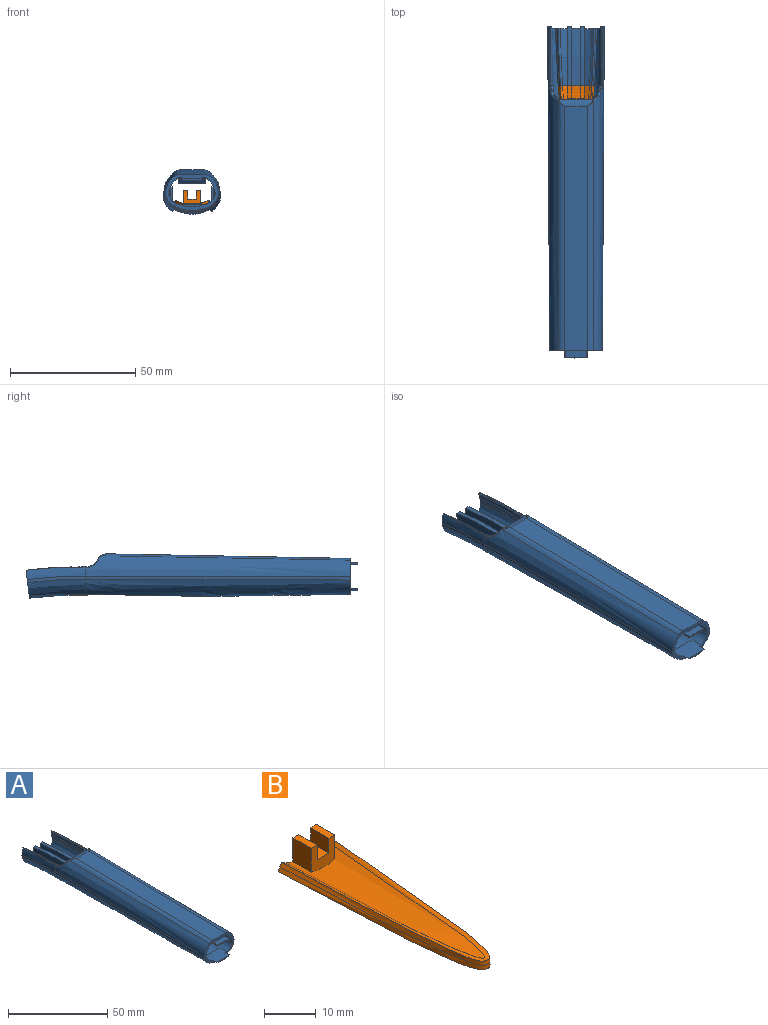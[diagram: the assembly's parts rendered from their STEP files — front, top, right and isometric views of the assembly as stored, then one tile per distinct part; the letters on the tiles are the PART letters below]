
ASSEMBLY  parts=2 mates=1
PART A: 134 faces, bbox 27x265.1x35.1 mm
  f0: bspline ~32.11x20.92mm, area 5.6mm2, adj f29,f36,f40,f76
  f1: plane 35.08x16.95mm, normal (0,0.02,-1), area 310.9mm2, adj f3,f5,f18,f20,f22,f67,f68,f70
  f2: plane 58.23x10.94mm, normal (0,0.02,-1), area 594.8mm2, adj f3,f5,f56,f57,f58,f60,f66
  f3: bspline ~105.7x8.16mm, area 859mm2, adj f1,f2,f4,f12,f13,f21,f22,f30
  f4: bspline ~228.99x1.34mm, area 68.2mm2, adj f3,f50,f56,f105
  f5: bspline ~105.7x8.16mm, area 859.1mm2, adj f1,f2,f6,f15,f16,f19,f20,f34
  f6: bspline ~85.15x0.93mm, area 68.2mm2, adj f5,f42,f56,f105
  f7: plane 97.19x9.34mm, normal (0,-0.02,1), area 895.6mm2, adj f10,f11,f18,f56
  f8: bspline ~228.99x9.18mm, area 873.6mm2, adj f11,f23,f24,f36,f56,f103
  f9: bspline ~105.7x8.28mm, area 873.5mm2, adj f10,f26,f27,f32,f56,f104
  f10: bspline ~141.43x3.43mm, area 259.1mm2, adj f7,f9,f28,f56
  f11: bspline ~141.43x3.43mm, area 259.1mm2, adj f7,f8,f25,f56
  f12: bspline ~228.99x1.34mm, area 19.6mm2, adj f3,f35,f52,f105
  f13: plane 2.29x0.93mm, normal (0,1,0), area 0.6mm2, adj f3,f14,f21,f23,f39,f40
  f14: cylinder r=5.4mm len=4.85mm, axis (-1,0,0), area 2.1mm2, adj f13,f18,f21,f23
  f15: plane 2.29x0.93mm, normal (0,1,0), area 0.6mm2, adj f5,f17,f19,f26,f38,f41
  f16: bspline ~228.99x1.34mm, area 19.6mm2, adj f5,f33,f45,f105
  f17: cylinder r=5.4mm len=4.85mm, axis (-1,0,0), area 2.1mm2, adj f15,f18,f19,f26
  f18: cylinder r=4mm len=16.08mm, axis (-1,0,0), area 40.3mm2, adj f1,f7,f14,f17,f20,f22,f24,f25
  f19: bspline ~6.36x4.3mm, area 6.3mm2, adj f5,f15,f17,f20
  f20: bspline ~3.28x2.53mm, area 2.3mm2, adj f1,f5,f18,f19
  f21: bspline ~6.36x4.3mm, area 6.3mm2, adj f3,f13,f14,f22
  f22: bspline ~3.42x2.68mm, area 2.3mm2, adj f1,f3,f18,f21
  f23: bspline ~6.57x4.71mm, area 4.1mm2, adj f8,f13,f14,f24,f29
  f24: bspline ~2.91x2.89mm, area 1.2mm2, adj f8,f18,f23,f25
  f25: bspline ~2.61x2.59mm, area 0.5mm2, adj f11,f18,f24
  f26: bspline ~6.57x4.71mm, area 4.1mm2, adj f9,f15,f17,f27,f31
  f27: bspline ~2.91x2.89mm, area 1.2mm2, adj f9,f18,f26,f28
  f28: bspline ~2.52x2.5mm, area 0.5mm2, adj f10,f18,f27
  f29: plane 0.41x0.34mm, normal (0,-1,0), area 0mm2, adj f0,f23,f36,f40
  f30: bspline ~23.58x3.47mm, area 44.4mm2, adj f3,f35,f39,f76
  f31: plane 0.41x0.34mm, normal (0,-1,0), area 0mm2, adj f26,f32,f37,f41
  f32: bspline ~32.11x6.34mm, area 91.7mm2, adj f9,f31,f37,f76,f124
  f33: bspline ~31.46x3.53mm, area 22.3mm2, adj f16,f34,f76,f128
  f34: bspline ~31.89x5.15mm, area 44.4mm2, adj f5,f33,f38,f76
  f35: bspline ~31.46x3.53mm, area 22.2mm2, adj f12,f30,f76,f122
  f36: bspline ~32.11x6.34mm, area 91.8mm2, adj f0,f8,f29,f76,f121
  f37: bspline ~32.11x20.92mm, area 5.6mm2, adj f31,f32,f41,f76
  f38: plane 23.86x2.59mm, normal (-1,0,0), area 33.8mm2, adj f15,f34,f41,f76
  f39: plane 23.86x2.59mm, normal (1,0,0), area 33.8mm2, adj f13,f30,f40,f76
  f40: bspline ~28.88x2.28mm, area 18.7mm2, adj f0,f13,f29,f39,f76
  f41: bspline ~28.88x2.28mm, area 18.7mm2, adj f15,f31,f37,f38,f76
  f42: plane 7.63x1.35mm, normal (0,-0.17,-0.98), area 7.1mm2, adj f5,f6,f43,f44,f45
  f43: plane 8.46x4.78mm, normal (-1,0,0), area 12mm2, adj f5,f42,f44,f45,f46,f47,f48
  f44: plane 3.3x0.89mm, normal (0,-0.98,0.17), area 1.8mm2, adj f5,f42,f43
  f45: plane 4.8x0.96mm, normal (0,0.98,-0.17), area 3.3mm2, adj f5,f16,f42,f43
  f46: plane 2.44x0.78mm, normal (0,0.98,-0.17), area 1.1mm2, adj f5,f43,f47
  f47: plane 6.27x1.11mm, normal (0,0.17,0.98), area 5.5mm2, adj f5,f43,f46,f48
  f48: plane 3.67x0.95mm, normal (0,-0.98,0.17), area 2.2mm2, adj f5,f43,f47
  f49: plane 8.46x4.78mm, normal (1,0,0), area 12mm2, adj f3,f50,f51,f52,f53,f54,f55
  f50: plane 7.63x1.35mm, normal (0,-0.17,-0.98), area 7.1mm2, adj f3,f4,f49,f51,f52
  f51: plane 3.3x0.89mm, normal (0,-0.98,0.17), area 1.8mm2, adj f3,f49,f50
  f52: plane 4.8x0.96mm, normal (0,0.98,-0.17), area 3.3mm2, adj f3,f12,f49,f50
  f53: plane 2.44x0.78mm, normal (0,0.98,-0.17), area 1.1mm2, adj f3,f49,f54
  f54: plane 6.27x1.11mm, normal (0,0.17,0.98), area 5.5mm2, adj f3,f49,f53,f55
  f55: plane 3.67x0.95mm, normal (0,-0.98,0.17), area 2.2mm2, adj f3,f49,f54
  f56: plane 24.01x17.36mm, normal (0,-1,0), area 74.5mm2, adj f2,f3,f4,f5,f6,f7,f8,f9
  f57: plane 8x1.09mm, normal (1,0,0), area 7.3mm2, adj f2,f56,f59,f60,f61,f62
  f58: plane 8x1.09mm, normal (-1,0,0), area 7.3mm2, adj f2,f56,f59,f60,f61,f62
  f59: plane 8x8mm, normal (0,0,-1), area 64mm2, adj f57,f58,f60,f62
  f60: plane 8x1.09mm, normal (0,1,0), area 8.8mm2, adj f2,f57,f58,f59
  f61: plane 8x3mm, normal (0,0,1), area 24mm2, adj f56,f57,f58,f62
  f62: plane 8x0.7mm, normal (0,-1,0), area 5.6mm2, adj f57,f58,f59,f61
  f63: plane 10.41x3.81mm, normal (-1,0,0), area 20.7mm2, adj f3,f64,f66,f67
  f64: plane 10.86x0.5mm, normal (0,0,-1), area 5.4mm2, adj f63,f65,f66,f67
  f65: plane 10.41x3.81mm, normal (1,0,0), area 20.7mm2, adj f5,f64,f66,f67
  f66: plane 10.87x9.9mm, normal (0,-0.34,-0.94), area 114.5mm2, adj f2,f63,f64,f65
  f67: plane 10.86x3.8mm, normal (0,1,0), area 17mm2, adj f1,f63,f64,f65,f68,f72
  f68: cylinder r=1.99mm len=12mm, axis (0,-1,0), area 135.3mm2, adj f1,f67,f70
  f69: cylinder r=1.75mm len=12mm, axis (0,-1,0), area 131.9mm2, adj f70,f71
  f70: plane 3.98x3.97mm, normal (0,1,0), area 2.8mm2, adj f1,f68,f69
  f71: plane 3.5x3.5mm, normal (0,1,0), area 9.6mm2, adj f69
  f72: cylinder r=1.99mm len=12mm, axis (0,-1,0), area 135.3mm2, adj f1,f67,f74
  f73: cylinder r=1.75mm len=12mm, axis (0,-1,0), area 131.9mm2, adj f74,f75
  f74: plane 3.98x3.97mm, normal (0,1,0), area 2.8mm2, adj f1,f72,f73
  f75: plane 3.5x3.5mm, normal (0,1,0), area 9.6mm2, adj f73
  f76: plane 23.73x12.13mm, normal (0,0.99,-0.13), area 90.5mm2, adj f0,f30,f32,f33,f34,f35,f36,f37
  f77: plane 6x1.06mm, normal (0,-0.17,-0.98), area 3.7mm2, adj f78,f88,f89,f90
  f78: plane 6.17x2.01mm, normal (-0.77,0.11,0.63), area 7.7mm2, adj f77,f79,f88,f90
  f79: plane 6x1.06mm, normal (0,0.17,0.98), area 3.6mm2, adj f78,f88,f90,f91
  f80: plane 6x1.06mm, normal (0,0.17,0.98), area 3.6mm2, adj f81,f92,f93,f94
  f81: plane 6.17x2.01mm, normal (0.77,0.11,0.63), area 7.7mm2, adj f80,f82,f92,f94
  f82: plane 6x1.06mm, normal (0,-0.17,-0.98), area 3.7mm2, adj f81,f92,f94,f95
  f83: plane 9.28x0.85mm, normal (0,-1,0), area 5.3mm2, adj f84,f97
  f84: extruded ~9.28x3mm, area 28.5mm2, adj f56,f83,f97
  f85: plane 1.05x0.03mm, normal (-1,0,0), area 0mm2, adj f86,f99,f100
  f86: offset ~230.99x17.57mm, area 401.1mm2, adj f85,f87,f98,f99,f100,f101
  f87: bspline ~11.21x7.08mm, area 0mm2, adj f86,f99,f101
  f88: plane 5.55x1.44mm, normal (0,0.98,-0.17), area 4.3mm2, adj f77,f78,f79,f89,f91,f105
  f89: plane 6.82x4.72mm, normal (-1,0,0), area 25.7mm2, adj f77,f88,f90,f105
  f90: plane 6.53x1.44mm, normal (0,-0.98,0.17), area 5.1mm2, adj f77,f78,f79,f89,f91,f105
  f91: plane 7.15x6.57mm, normal (1,0,0), area 37.2mm2, adj f79,f88,f90,f105
  f92: plane 5.55x1.44mm, normal (0,0.98,-0.17), area 4.3mm2, adj f80,f81,f82,f93,f95,f105
  f93: plane 7.15x6.57mm, normal (-1,0,0), area 37.2mm2, adj f80,f92,f94,f105
  f94: plane 6.54x1.44mm, normal (0,-0.98,0.17), area 5.1mm2, adj f80,f81,f82,f93,f95,f105
  f95: plane 6.82x4.72mm, normal (1,0,0), area 25.7mm2, adj f82,f92,f94,f105
  f96: plane 11.24x1.13mm, normal (0,1,0), area 8.7mm2, adj f97,f105
  f97: plane 11.24x8mm, normal (0,0,1), area 83.4mm2, adj f56,f83,f84,f96,f105
  f98: bspline ~56.35x13.51mm, area 99mm2, adj f86,f102,f105,f106
  f99: plane 7.16x6.4mm, normal (0,-1,0), area 33.7mm2, adj f85,f86,f87,f111,f112,f113,f114,f131
  f100: bspline ~2.99x2.01mm, area 2.7mm2, adj f85,f86,f107,f123
  f101: bspline ~3.05x2.05mm, area 2.8mm2, adj f86,f87,f108,f129
  f102: bspline ~1.39x1.39mm, area 1mm2, adj f98,f105,f107,f117
  f103: bspline ~228.99x1.71mm, area 140.7mm2, adj f8,f56,f109,f121
  f104: bspline ~228.99x1.71mm, area 140.7mm2, adj f9,f56,f109,f124
  f105: bspline ~105.7x19.67mm, area 2007.8mm2, adj f4,f6,f12,f16,f56,f88,f89,f90
  f106: bspline ~1.39x1.39mm, area 1mm2, adj f98,f105,f108,f127
  f107: bspline ~1.38x1.38mm, area 1mm2, adj f100,f102,f115,f116
  f108: bspline ~1.38x1.38mm, area 1mm2, adj f101,f106,f125,f126
  f109: bspline ~105.7x22.25mm, area 2448.7mm2, adj f56,f103,f104,f118,f120,f130
  f110: bspline ~228.99x15.57mm, area 444.2mm2, adj f118,f119
  f111: plane 23.42x4.77mm, normal (-1,0,0), area 81.3mm2, adj f76,f99,f112,f133
  f112: bspline ~31.04x3.2mm, area 73.7mm2, adj f76,f99,f111,f113
  f113: plane 23.42x4.77mm, normal (1,0,0), area 81.3mm2, adj f76,f99,f112,f114
  f114: bspline ~31.61x2.6mm, area 37.5mm2, adj f76,f99,f113,f131
  f115: offset ~28x4.01mm, area 23mm2, adj f76,f107,f116,f123
  f116: bspline ~25.76x1.8mm, area 23mm2, adj f76,f107,f115,f117
  f117: offset ~28.28x3.89mm, area 21.6mm2, adj f76,f102,f105,f116,f122
  f118: extruded ~71.85x28.66mm, area 193.5mm2, adj f76,f109,f110,f119,f120,f130
  f119: bspline ~30.89x18.04mm, area 337.3mm2, adj f76,f110,f118
  f120: bspline ~23.16x7.13mm, area 165.1mm2, adj f76,f109,f118,f121
  f121: bspline ~31.48x3.78mm, area 28.4mm2, adj f36,f76,f103,f120
  f122: bspline ~23.18x5.28mm, area 98.7mm2, adj f35,f76,f105,f117
  f123: offset ~35x11.55mm, area 68.4mm2, adj f76,f100,f115,f131
  f124: bspline ~23.31x2.49mm, area 28.5mm2, adj f32,f76,f104,f130
  f125: offset ~28.01x4.02mm, area 23mm2, adj f76,f108,f126,f129
  f126: bspline ~25.45x1.91mm, area 23mm2, adj f76,f108,f125,f127
  f127: offset ~24.84x3.64mm, area 21.6mm2, adj f76,f105,f106,f126,f128
  f128: bspline ~31.31x7.67mm, area 97.2mm2, adj f33,f76,f105,f127
  f129: offset ~35x11.55mm, area 69.6mm2, adj f76,f101,f125,f132
  f130: bspline ~31.28x9.39mm, area 163.7mm2, adj f76,f109,f118,f124
  f131: plane 24.12x7.67mm, normal (-1,0,0), area 130.9mm2, adj f76,f99,f114,f123
  f132: bspline ~31.61x9.4mm, area 131.9mm2, adj f76,f99,f129,f133
  f133: bspline ~31.61x2.6mm, area 37.5mm2, adj f76,f99,f111,f132
PART B: 29 faces, bbox 19.6x234.9x12.2 mm
  f0: bspline ~0.97x0.26mm, area 0mm2, adj f1,f4,f5,f6
  f1: bspline ~2.99x2.01mm, area 2.8mm2, adj f0,f5,f6,f9
  f2: bspline ~3.05x2.05mm, area 2.9mm2, adj f3,f5,f6,f7
  f3: bspline ~0.97x0.26mm, area 0mm2, adj f2,f4,f5,f6
  f4: bspline ~6.4x1.38mm, area 6.2mm2, adj f0,f3,f5,f19
  f5: offset ~151.53x19.57mm, area 337.7mm2, adj f0,f1,f2,f3,f4,f8,f20,f26
  f6: offset ~230.99x17.57mm, area 371.1mm2, adj f0,f1,f2,f3,f13,f16,f17,f18
  f7: bspline ~1.38x1.38mm, area 1mm2, adj f2,f8,f10,f14
  f8: bspline ~49.81x12.56mm, area 100.5mm2, adj f5,f7,f9,f10
  f9: bspline ~1.38x1.38mm, area 1mm2, adj f1,f8,f10,f12
  f10: offset ~52.81x14.13mm, area 101.5mm2, adj f7,f8,f9,f11
  f11: bspline ~49.83x14.68mm, area 102.4mm2, adj f10,f12,f14,f15
  f12: bspline ~1.38x1.38mm, area 1mm2, adj f9,f11,f13,f15
  f13: bspline ~48.89x12.98mm, area 100mm2, adj f6,f12,f14,f15
  f14: bspline ~1.38x1.38mm, area 1mm2, adj f7,f11,f13,f15
  f15: offset ~51.82x15.62mm, area 100.7mm2, adj f11,f12,f13,f14
  f16: plane 6.41x0.5mm, normal (0,-1,0), area 0.4mm2, adj f6,f17,f18,f19
  f17: plane 5x0.07mm, normal (-1,0,0), area 0.2mm2, adj f6,f16,f19
  f18: plane 5x0.07mm, normal (1,0,0), area 0.2mm2, adj f6,f16,f19
  f19: extruded ~6.4x5mm, area 32.4mm2, adj f4,f16,f17,f18
  f20: plane 5.7x5mm, normal (1,0,0), area 28.3mm2, adj f5,f21,f27,f28
  f21: plane 5x1.6mm, normal (0,0,1), area 8mm2, adj f20,f22,f27,f28
  f22: plane 5x3.5mm, normal (-1,0,0), area 17.5mm2, adj f21,f23,f27,f28
  f23: plane 5x3.2mm, normal (0,0,1), area 16mm2, adj f22,f24,f27,f28
  f24: plane 5x3.5mm, normal (1,0,0), area 17.5mm2, adj f23,f25,f27,f28
  f25: plane 5x1.6mm, normal (0,0,1), area 8mm2, adj f24,f26,f27,f28
  f26: plane 5.7x5mm, normal (-1,0,0), area 28.3mm2, adj f5,f25,f27,f28
  f27: plane 6.4x6.09mm, normal (0,-1,0), area 26.8mm2, adj f5,f20,f21,f22,f23,f24,f25,f26
  f28: plane 6.4x6.16mm, normal (0,1,0), area 27.2mm2, adj f5,f20,f21,f22,f23,f24,f25,f26
PLACE A t=(-57.26,106.35,-29.72)mm
PLACE B t=(-57.26,106.35,-29.72)mm
MATE fastened B.f28 <-> A.f99  axis (0,1,0) through (-54.06,-15.16,-28.91)mm
